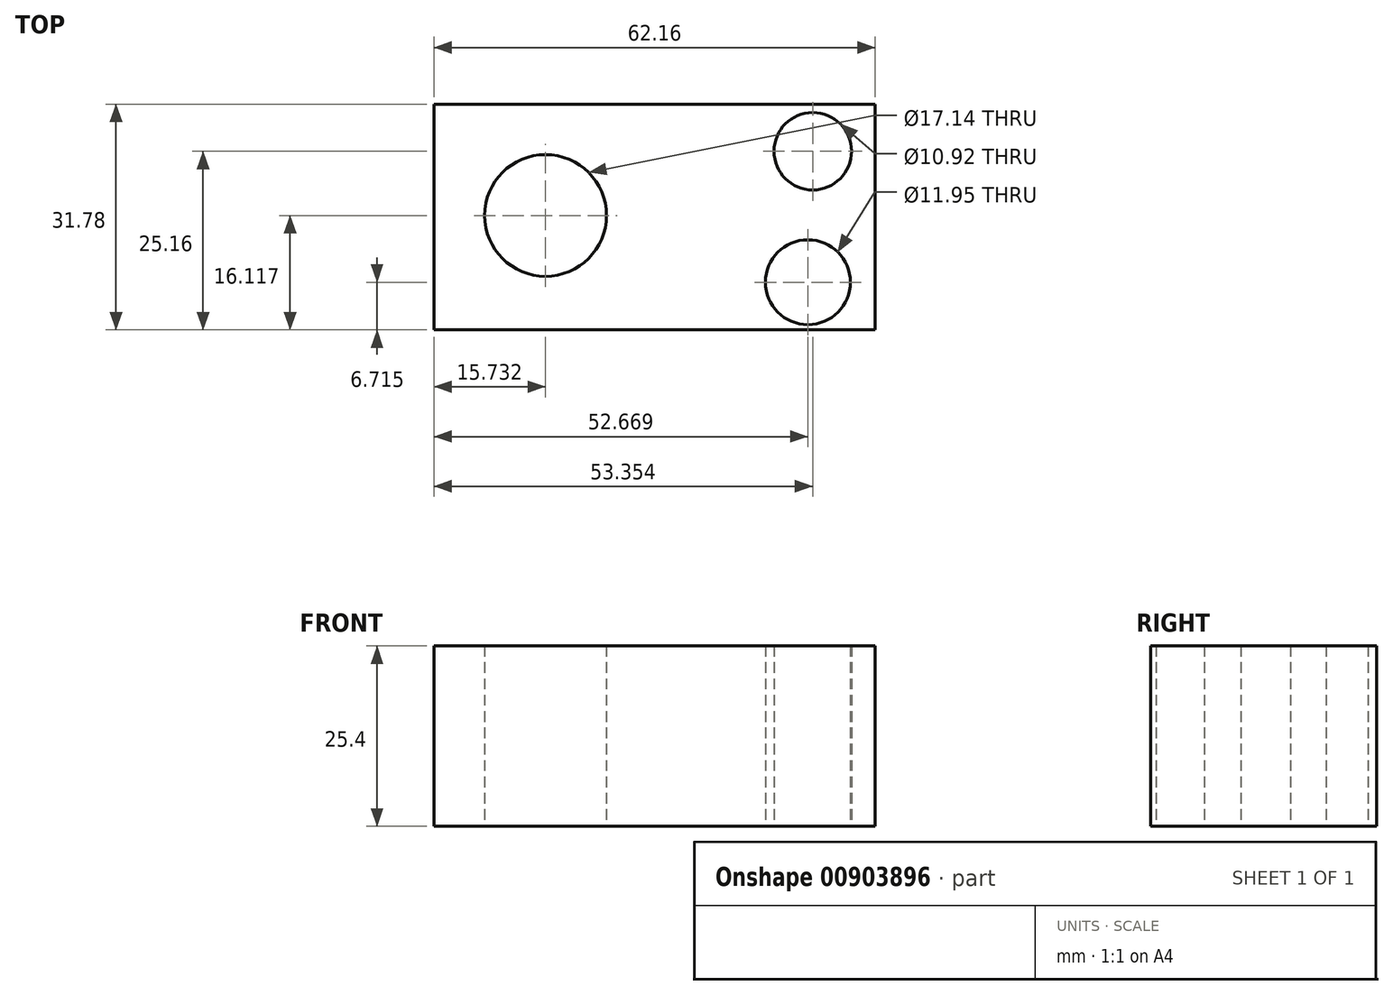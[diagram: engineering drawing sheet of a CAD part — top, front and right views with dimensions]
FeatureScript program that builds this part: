
annotation { "Feature Type Name" : "Feature", "Feature Type Description" : "" }
export const myFeature = defineFeature(function(context is Context, id is Id, definition is map)
    precondition{}
    {
        {
            var Q0;
            Q0=qCreatedBy(makeId("Top.planeOp"),FACE);
            var sketch = newSketch(context, id + "F0", { "sketchPlane" : qUnion([Q0])});
            skLineSegment(sketch, "E0.bottom", {"start": v(-88, -24.5) * mm, "end": v(-25.84, -24.5) * mm});
            skLineSegment(sketch, "E0.top", {"start": v(-88, -56.28) * mm, "end": v(-25.84, -56.28) * mm});
            skLineSegment(sketch, "E0.left", {"start": v(-88, -24.5) * mm, "end": v(-88, -56.28) * mm});
            skLineSegment(sketch, "E0.right", {"start": v(-25.84, -24.5) * mm, "end": v(-25.84, -56.28) * mm});
            skCircle(sketch, "E1", {"center": v(-72.27, -40.16) * mm, "radius": 8.57 * mm});
            skCircle(sketch, "E2", {"center": v(-34.65, -31.12) * mm, "radius": 5.46 * mm});
            skCircle(sketch, "E3", {"center": v(-35.33, -49.57) * mm, "radius": 5.97 * mm});
            skSolve(sketch);
        }
        {
            var Q0;
            Q0 = qSketchRegion(id + "F0", true);
            extrude(context, id + "F1", {"entities" : qUnion([Q0]), "depth" : 6.35 * mm, "offsetDistance" : 25.4 * mm});
        }
        {
            var Q0;
            Q0 = qSketchRegion(id + "F0", true);
            extrude(context, id + "F2", {"entities" : qUnion([Q0]), "operationType" : NewBodyOperationType.ADD, "depth" : 25.4 * mm, "offsetDistance" : 25.4 * mm});
        }
    });
